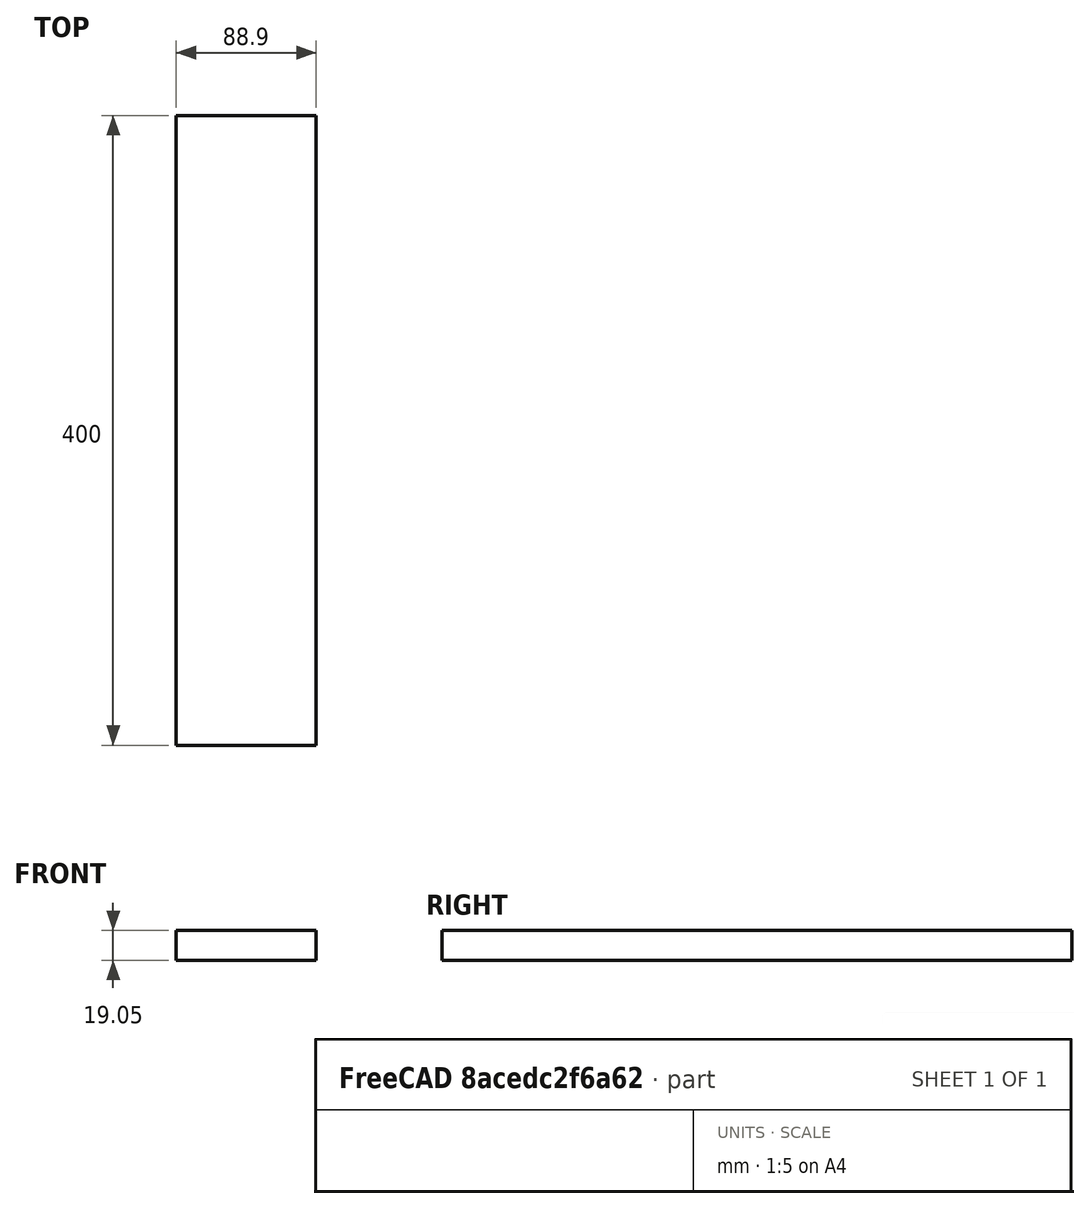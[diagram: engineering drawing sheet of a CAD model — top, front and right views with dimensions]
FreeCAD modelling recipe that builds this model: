
FCSTD DOCUMENT  (FreeCAD 0.19R24291 (Git))
Label: board
License: All rights reserved
LicenseURL: http://en.wikipedia.org/wiki/All_rights_reserved
objects: Sketcher::SketchObject×1, PartDesign::Pad×1, PartDesign::Body×1
note: 4 computed .brp shape members not serialized (recipe doc carries the construction recipe); baked Part::Feature solids carry a one-line shape summary decoded from their .brp

FEATURE [Sketcher::SketchObject] Sketch
  FullyConstrained = true
  MapMode = 5
  Support = -> [XY_Plane]
  expr: Constraints[9] = 3.5 * 25.4
  sketch-geometry (4):
    g0: LineSegment StartX=0 StartY=0 StartZ=0 EndX=88.9 EndY=0 EndZ=0
    g1: LineSegment StartX=88.9 StartY=0 StartZ=0 EndX=88.9 EndY=400 EndZ=0
    g2: LineSegment StartX=88.9 StartY=400 StartZ=0 EndX=0 EndY=400 EndZ=0
    g3: LineSegment StartX=0 StartY=400 StartZ=0 EndX=0 EndY=0 EndZ=0
  constraints (11):
    c: Coincident(g0,g1)
    c: Coincident(g1,g2)
    c: Coincident(g2,g3)
    c: Coincident(g3,g0)
    c: Horizontal(g0)
    c: Horizontal(g2)
    c: Vertical(g1)
    c: Vertical(g3)
    c: Coincident(g0,g-1)
    c: DistanceX(g0,g0) = 88.9
    c: DistanceY(g3,g3) = 400
FEATURE [PartDesign::Pad] Pad
  Direction = (1,1,1)
  Length = 19.05
  Length2 = 100
  Profile = -> Sketch
  Type = 0
FEATURE [PartDesign::Body] Body
  Group = -> [Sketch,Pad]
  Origin = -> Origin
  Tip = -> Pad
